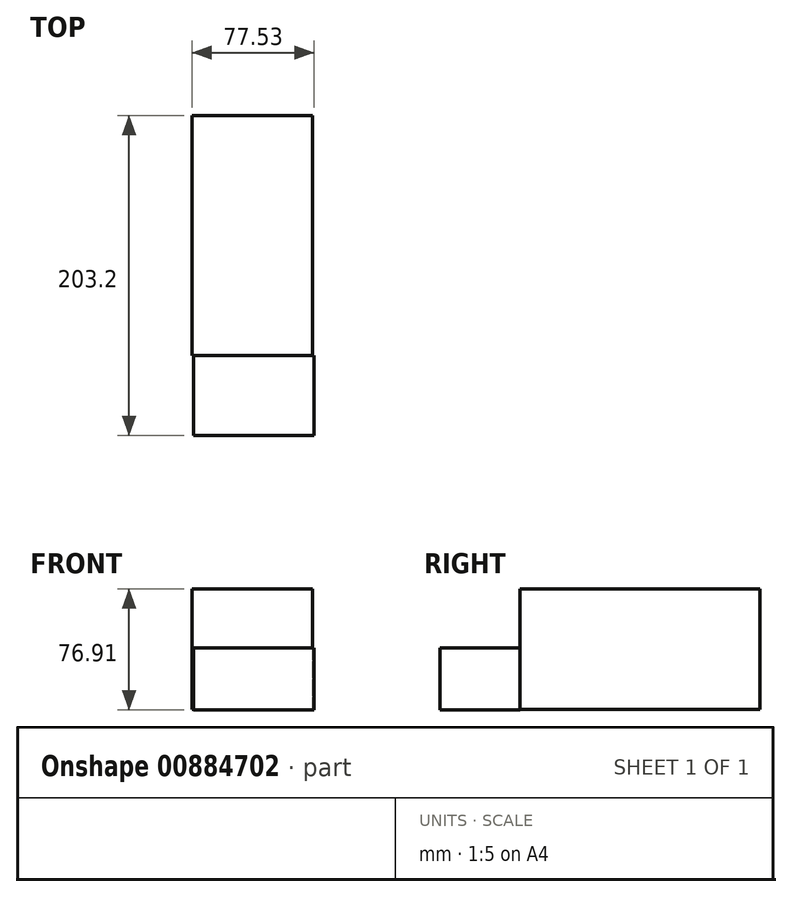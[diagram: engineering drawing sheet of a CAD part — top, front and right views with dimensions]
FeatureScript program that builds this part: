
annotation { "Feature Type Name" : "Feature", "Feature Type Description" : "" }
export const myFeature = defineFeature(function(context is Context, id is Id, definition is map)
    precondition{}
    {
        {
            var Q0;
            Q0=qCreatedBy(makeId("Front.planeOp"),FACE);
            var sketch = newSketch(context, id + "F0", { "sketchPlane" : qUnion([Q0])});
            skLineSegment(sketch, "E0.bottom", {"start": v(-26.83, 30.24) * mm, "end": v(49.77, 30.24) * mm});
            skLineSegment(sketch, "E0.top", {"start": v(-26.83, -46.36) * mm, "end": v(49.77, -46.36) * mm});
            skLineSegment(sketch, "E0.left", {"start": v(-26.83, 30.24) * mm, "end": v(-26.83, -46.36) * mm});
            skLineSegment(sketch, "E0.right", {"start": v(49.77, 30.24) * mm, "end": v(49.77, -46.36) * mm});
            skSolve(sketch);
        }
        {
            var Q0;
            Q0=qSketchRegion(id+"F0",true);
            extrude(context, id + "F1", {"entities" : qUnion([Q0]), "oppositeDirection" : true, "depth" : 152.4 * mm, "offsetDistance" : 25.4 * mm});
        }
        {
            var Q0;
            Q0=qCreatedBy(makeId("Front.planeOp"),FACE);
            var sketch = newSketch(context, id + "F2", { "sketchPlane" : qUnion([Q0])});
            skLineSegment(sketch, "E1.bottom", {"start": v(-25.9, -7.29) * mm, "end": v(50.7, -7.29) * mm});
            skLineSegment(sketch, "E1.top", {"start": v(-25.9, -46.67) * mm, "end": v(50.7, -46.67) * mm});
            skLineSegment(sketch, "E1.left", {"start": v(-25.9, -7.29) * mm, "end": v(-25.9, -46.67) * mm});
            skLineSegment(sketch, "E1.right", {"start": v(50.7, -7.29) * mm, "end": v(50.7, -46.67) * mm});
            skSolve(sketch);
        }
        {
            var Q0;
            Q0=qSketchRegion(id+"F2",true);
            extrude(context, id + "F3", {"entities" : qUnion([Q0]), "operationType" : NewBodyOperationType.ADD, "depth" : 50.8 * mm, "offsetDistance" : 25.4 * mm});
        }
    });
